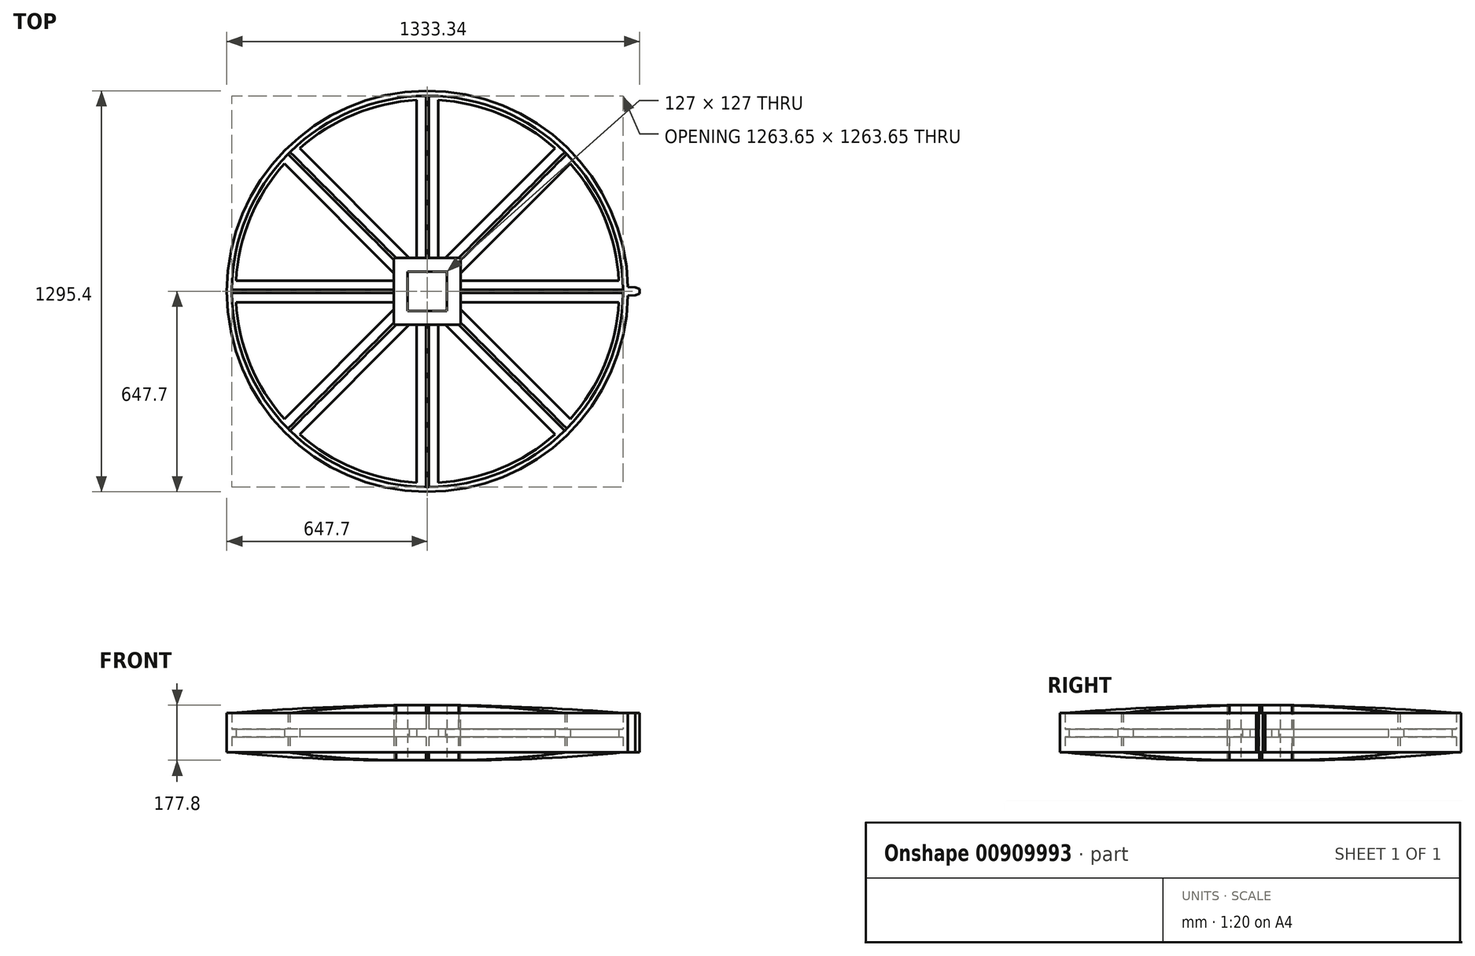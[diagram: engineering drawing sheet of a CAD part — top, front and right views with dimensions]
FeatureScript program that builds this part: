
annotation { "Feature Type Name" : "Feature", "Feature Type Description" : "" }
export const myFeature = defineFeature(function(context is Context, id is Id, definition is map)
    precondition{}
    {
        {
            var Q0;
            Q0=qCreatedBy(makeId("Front.planeOp"),FACE);
            var sketch = newSketch(context, id + "F0", { "sketchPlane" : qUnion([Q0])});
            skLineSegment(sketch, "E0.bottom", {"start": v(0, -88.9) * mm, "end": v(107.95, -88.9) * mm});
            skLineSegment(sketch, "E0.top", {"start": v(0, 88.9) * mm, "end": v(107.95, 88.9) * mm});
            skLineSegment(sketch, "E0.left", {"start": v(0, -88.9) * mm, "end": v(0, 88.9) * mm});
            skLineSegment(sketch, "E0.right", {"start": v(107.95, -88.9) * mm, "end": v(107.95, 88.9) * mm});
            skLineSegment(sketch, "E1.bottom", {"start": v(631.82, -63.5) * mm, "end": v(647.7, -63.5) * mm});
            skLineSegment(sketch, "E1.top", {"start": v(631.82, 63.5) * mm, "end": v(647.7, 63.5) * mm});
            skLineSegment(sketch, "E1.left", {"start": v(631.82, -63.5) * mm, "end": v(631.82, 63.5) * mm});
            skLineSegment(sketch, "E1.right", {"start": v(647.7, -63.5) * mm, "end": v(647.7, 63.5) * mm});
            skLineSegment(sketch, "E2", {"start": v(63.5, 88.9) * mm, "end": v(63.5, -88.9) * mm});
            skLineSegment(sketch, "E3", {"start": v(63.5, 12.5) * mm, "end": v(631.82, 12.5) * mm});
            skLineSegment(sketch, "E4", {"start": v(63.5, -12.9) * mm, "end": v(631.82, -12.9) * mm});
            skLineSegment(sketch, "E5", {"start": v(0, -88.9) * mm, "end": v(0, -224.91) * mm, "construction": true});
            skArc(sketch, "E6", {"start": v(631.82, 63.5) * mm, "mid": v(370.1, 80.7) * mm, "end": v(107.95, 88.9) * mm});
            skPoint(sketch, "E7", {"position": v(0, 0) * mm});
            skLineSegment(sketch, "E8", {"start": v(631.82, 0) * mm, "end": v(0, 0) * mm, "construction": true});
            skArc(sketch, "E9", {"start": v(107.95, -88.9) * mm, "mid": v(370.2, -82.55) * mm, "end": v(631.83, -63.5) * mm});
            skLineSegment(sketch, "E10", {"start": v(619.12, 12.5) * mm, "end": v(619.12, -12.9) * mm});
            skSolve(sketch);
        }
        {
            var Q0;
            {var subQ0=sQuery(id+"F0.wireOp",EDGE,"E0.left");Q0=makeQuery(id+"F0.imprint","IMPRINT",FACE,{"disambiguationData":[TD([[makeQuery(id+"F0.imprint","IMPRINT",EDGE,{"derivedFrom":subQ0}),-1.0]])]});}
            var Q1;
            {var subQ6=sQuery(id+"F0.wireOp",EDGE,"E2");Q1=makeQuery(id+"F0.imprint","IMPRINT",FACE,{"disambiguationData":[TD([[makeQuery(id+"F0.imprint","IMPRINT",EDGE,{"derivedFrom":subQ6}),1.0]])]});}
            var Q2;
            Q2=sQuery(id+"F0.wireOp",EDGE,"E0.left");
            revolve(context, id + "F1", {"surfaceOperationType" : NewSurfaceOperationType.NEW, "entities" : qUnion([Q0, Q1]), "axis" : qUnion([Q2]), "revolveType" : RevolveType.SYMMETRIC, "angle" : 45 * degree});
        }
        {
            var Q0;
            {var subQ0=sQuery(id+"F0.wireOp",EDGE,"E4");var subQ1=sQuery(id+"F0.wireOp",EDGE,"E0.right");var subQ2=makeQuery(id+"F0.imprint","INTERSECT",VERTEX,{"derivedFrom":[subQ1,subQ0]});Q0=makeQuery(id+"F0.imprint","IMPRINT",FACE,{"disambiguationData":[TD([[makeQuery(id+"F0.imprint","IMPRINT",EDGE,{"disambiguationData":[TD([[subQ2,-1.0]])],"derivedFrom":subQ1}),-1.0]])]});}
            var Q1;
            {var subQ0=sQuery(id+"F0.wireOp",EDGE,"E4");var subQ1=sQuery(id+"F0.wireOp",EDGE,"E0.right");var subQ2=makeQuery(id+"F0.imprint","INTERSECT",VERTEX,{"derivedFrom":[subQ1,subQ0]});Q1=makeQuery(id+"F0.imprint","IMPRINT",FACE,{"disambiguationData":[TD([[makeQuery(id+"F0.imprint","IMPRINT",EDGE,{"disambiguationData":[TD([[subQ2,-1.0]])],"derivedFrom":subQ1}),1.0]])]});}
            extrude(context, id + "F2", {"entities" : qUnion([Q0, Q1]), "operationType" : NewBodyOperationType.ADD, "depth" : 69.85 * mm, "offsetDistance" : 25 * mm, "symmetric" : true});
        }
        {
            var Q0;
            {var subQ3=sQuery(id+"F0.wireOp",EDGE,"E1.bottom");Q0=makeQuery(id+"F0.imprint","IMPRINT",FACE,{"disambiguationData":[TD([[makeQuery(id+"F0.imprint","IMPRINT",EDGE,{"derivedFrom":subQ3}),1.0]])]});}
            var Q1;
            {var subQ5=sQuery(id+"F0.wireOp",EDGE,"E10");Q1=makeQuery(id+"F0.imprint","IMPRINT",FACE,{"disambiguationData":[TD([[makeQuery(id+"F0.imprint","IMPRINT",EDGE,{"derivedFrom":subQ5}),1.0]])]});}
            var Q2;
            Q2=sQuery(id+"F0.wireOp",EDGE,"E0.left");
            revolve(context, id + "F3", {"operationType" : NewBodyOperationType.ADD, "surfaceOperationType" : NewSurfaceOperationType.NEW, "entities" : qUnion([Q0, Q1]), "axis" : qUnion([Q2]), "revolveType" : RevolveType.SYMMETRIC, "angle" : 45 * degree});
        }
        {
            var Q0;
            {var subQ1=sQuery(id+"F0.wireOp",EDGE,"E0.top");var subQ3=sQuery(id+"F0.wireOp",EDGE,"E2");var subQ4=makeQuery(id+"F0.imprint","INTERSECT",VERTEX,{"derivedFrom":[subQ1,subQ3]});Q0=makeQuery(id+"F0.imprint","IMPRINT",FACE,{"disambiguationData":[TD([[makeQuery(id+"F0.imprint","IMPRINT",EDGE,{"disambiguationData":[TD([[subQ4,-1.0]])],"derivedFrom":subQ3}),1.0]])]});}
            var Q1;
            {var subQ1=sQuery(id+"F0.wireOp",EDGE,"E0.bottom");var subQ3=sQuery(id+"F0.wireOp",EDGE,"E2");var subQ4=makeQuery(id+"F0.imprint","INTERSECT",VERTEX,{"derivedFrom":[subQ1,subQ3]});Q1=makeQuery(id+"F0.imprint","IMPRINT",FACE,{"disambiguationData":[TD([[makeQuery(id+"F0.imprint","IMPRINT",EDGE,{"disambiguationData":[TD([[subQ4,1.0]])],"derivedFrom":subQ3}),1.0]])]});}
            var Q2;
            {var subQ0=sQuery(id+"F0.wireOp",EDGE,"E6");Q2=makeQuery(id+"F0.imprint","IMPRINT",FACE,{"disambiguationData":[TD([[makeQuery(id+"F0.imprint","IMPRINT",EDGE,{"derivedFrom":subQ0}),1.0]])]});}
            var Q3;
            {var subQ0=sQuery(id+"F0.wireOp",EDGE,"E9");Q3=makeQuery(id+"F0.imprint","IMPRINT",FACE,{"disambiguationData":[TD([[makeQuery(id+"F0.imprint","IMPRINT",EDGE,{"derivedFrom":subQ0}),1.0]])]});}
            extrude(context, id + "F4", {"entities" : qUnion([Q0, Q1, Q2, Q3]), "operationType" : NewBodyOperationType.ADD, "depth" : 9.53 * mm, "offsetDistance" : 25 * mm, "symmetric" : true});
        }
        {
            var Q0;
            Q0=makeQuery(id+"F1.opRevolve","SWEPT_BODY",BODY,{"disambiguationData":[OSD([sQuery(id+"F0.wireOp",EDGE,"E0.bottom"),sQuery(id+"F0.wireOp",EDGE,"E0.top"),sQuery(id+"F0.wireOp",EDGE,"E0.left"),sQuery(id+"F0.wireOp",EDGE,"E0.right")])]});
            var Q1;
            Q1=sQuery(id+"F0.wireOp",EDGE,"E0.left");
            circularPattern(context, id + "F5", {"operationType" : NewBodyOperationType.ADD, "entities" : qUnion([Q0]), "axis" : qUnion([Q1]), "angle" : 360 * degree, "instanceCount" : 8, "equalSpace" : true});
        }
        {
            var Q0;
            {var subQ0=makeQuery(id+"F3.opRevolve","SWEPT_FACE",FACE,{"disambiguationData":[OSD([sQuery(id+"F0.wireOp",EDGE,"E1.top")])]});Q0=makeQuery(id+"F5.boolean.opBoolean","MERGE",FACE,{"derivedFrom":[subQ0,makeQuery(id+"F5.opPattern","COPY",FACE,{"derivedFrom":subQ0,"instanceName":"1"}),makeQuery(id+"F5.opPattern","COPY",FACE,{"derivedFrom":subQ0,"instanceName":"2"}),makeQuery(id+"F5.opPattern","COPY",FACE,{"derivedFrom":subQ0,"instanceName":"3"}),makeQuery(id+"F5.opPattern","COPY",FACE,{"derivedFrom":subQ0,"instanceName":"4"}),makeQuery(id+"F5.opPattern","COPY",FACE,{"derivedFrom":subQ0,"instanceName":"5"}),makeQuery(id+"F5.opPattern","COPY",FACE,{"derivedFrom":subQ0,"instanceName":"6"}),makeQuery(id+"F5.opPattern","COPY",FACE,{"derivedFrom":subQ0,"instanceName":"7"})]});}
            var sketch = newSketch(context, id + "F6", { "sketchPlane" : qUnion([Q0])});
            skLineSegment(sketch, "E11", {"start": v(647.54, 14.29) * mm, "end": v(671.86, 12.16) * mm});
            skLineSegment(sketch, "E12", {"start": v(671.86, 12.16) * mm, "end": v(685.64, 7.14) * mm});
            skLineSegment(sketch, "E13", {"start": v(685.64, 7.14) * mm, "end": v(685.64, -7.14) * mm});
            skLineSegment(sketch, "E14", {"start": v(685.64, -7.14) * mm, "end": v(671.86, -12.16) * mm});
            skLineSegment(sketch, "E15", {"start": v(671.86, -12.16) * mm, "end": v(647.54, -14.29) * mm});
            skLineSegment(sketch, "E16", {"start": v(0, 0) * mm, "end": v(685.64, 0) * mm, "construction": true});
            skLineSegment(sketch, "E17", {"start": v(647.54, 14.29) * mm, "end": v(647.54, -14.29) * mm});
            skSolve(sketch);
        }
        {
            var Q0;
            {var subQ0=sQuery(id+"F6.wireOp",EDGE,"E11");Q0=makeQuery(id+"F6.imprint","IMPRINT",FACE,{"disambiguationData":[TD([[makeQuery(id+"F6.imprint","IMPRINT",EDGE,{"derivedFrom":subQ0}),-1.0]])]});}
            var Q1;
            {var subQ0=sQuery(id+"F0.wireOp",EDGE,"E0.bottom");var subQ1=makeQuery(id+"F4.boolean.opBoolean","MERGE",FACE,{"derivedFrom":[makeQuery(id+"F1.opRevolve","SWEPT_FACE",FACE,{"disambiguationData":[OSD([subQ0])]}),makeQuery(id+"F3.opRevolve","SWEPT_FACE",FACE,{"disambiguationData":[OSD([sQuery(id+"F0.wireOp",EDGE,"E1.bottom")])]}),makeQuery(id+"F4.opExtrude","SWEPT_FACE",FACE,{"disambiguationData":[OSD([subQ0,sQuery(id+"F0.wireOp",EDGE,"D5k9asr0-8ta1-f4uu-XxQ3-tXAVFih4KlHv")])]})]});Q1=makeQuery(id+"F5.boolean.opBoolean","MERGE",FACE,{"derivedFrom":[subQ1,makeQuery(id+"F5.opPattern","COPY",FACE,{"derivedFrom":subQ1,"instanceName":"1"}),makeQuery(id+"F5.opPattern","COPY",FACE,{"derivedFrom":subQ1,"instanceName":"2"}),makeQuery(id+"F5.opPattern","COPY",FACE,{"derivedFrom":subQ1,"instanceName":"3"}),makeQuery(id+"F5.opPattern","COPY",FACE,{"derivedFrom":subQ1,"instanceName":"4"}),makeQuery(id+"F5.opPattern","COPY",FACE,{"derivedFrom":subQ1,"instanceName":"5"}),makeQuery(id+"F5.opPattern","COPY",FACE,{"derivedFrom":subQ1,"instanceName":"6"}),makeQuery(id+"F5.opPattern","COPY",FACE,{"derivedFrom":subQ1,"instanceName":"7"})]});}
            extrude(context, id + "F7", {"entities" : qUnion([Q0]), "operationType" : NewBodyOperationType.ADD, "oppositeDirection" : true, "depth" : 127 * mm, "endBoundEntityFace" : qUnion([Q1]), "offsetDistance" : 25 * mm});
        }
        {
            var Q0;
            {var subQ0=sQuery(id+"F0.wireOp",EDGE,"E0.bottom");var subQ1=makeQuery(id+"F4.boolean.opBoolean","MERGE",FACE,{"derivedFrom":[makeQuery(id+"F1.opRevolve","SWEPT_FACE",FACE,{"disambiguationData":[OSD([subQ0])]}),makeQuery(id+"F3.opRevolve","SWEPT_FACE",FACE,{"disambiguationData":[OSD([sQuery(id+"F0.wireOp",EDGE,"E1.bottom")])]}),makeQuery(id+"F4.opExtrude","SWEPT_FACE",FACE,{"disambiguationData":[OSD([subQ0,sQuery(id+"F0.wireOp",EDGE,"D5k9asr0-8ta1-f4uu-XxQ3-tXAVFih4KlHv")])]})]});Q0=makeQuery(id+"F5.boolean.opBoolean","MERGE",FACE,{"derivedFrom":[subQ1,makeQuery(id+"F5.opPattern","COPY",FACE,{"derivedFrom":subQ1,"instanceName":"1"}),makeQuery(id+"F5.opPattern","COPY",FACE,{"derivedFrom":subQ1,"instanceName":"2"}),makeQuery(id+"F5.opPattern","COPY",FACE,{"derivedFrom":subQ1,"instanceName":"3"}),makeQuery(id+"F5.opPattern","COPY",FACE,{"derivedFrom":subQ1,"instanceName":"4"}),makeQuery(id+"F5.opPattern","COPY",FACE,{"derivedFrom":subQ1,"instanceName":"5"}),makeQuery(id+"F5.opPattern","COPY",FACE,{"derivedFrom":subQ1,"instanceName":"6"}),makeQuery(id+"F5.opPattern","COPY",FACE,{"derivedFrom":subQ1,"instanceName":"7"})]});}
            var sketch = newSketch(context, id + "F8", { "sketchPlane" : qUnion([Q0])});
            skLineSegment(sketch, "E18.bottom", {"start": v(-63.5, 63.5) * mm, "end": v(63.5, 63.5) * mm});
            skLineSegment(sketch, "E18.top", {"start": v(-63.5, -63.5) * mm, "end": v(63.5, -63.5) * mm});
            skLineSegment(sketch, "E18.left", {"start": v(-63.5, 63.5) * mm, "end": v(-63.5, -63.5) * mm});
            skLineSegment(sketch, "E18.right", {"start": v(63.5, 63.5) * mm, "end": v(63.5, -63.5) * mm});
            skLineSegment(sketch, "E19", {"start": v(-63.5, 63.5) * mm, "end": v(63.5, -63.5) * mm, "construction": true});
            skLineSegment(sketch, "E20", {"start": v(63.5, 63.5) * mm, "end": v(-63.5, -63.5) * mm, "construction": true});
            skLineSegment(sketch, "E21.bottom", {"start": v(-107.95, -107.95) * mm, "end": v(107.95, -107.95) * mm});
            skLineSegment(sketch, "E21.top", {"start": v(-107.95, 107.95) * mm, "end": v(107.95, 107.95) * mm});
            skLineSegment(sketch, "E21.left", {"start": v(-107.95, -107.95) * mm, "end": v(-107.95, 107.95) * mm});
            skLineSegment(sketch, "E21.right", {"start": v(107.95, -107.95) * mm, "end": v(107.95, 107.95) * mm});
            skSolve(sketch);
        }
        {
            var Q0;
            {var subQ2=sQuery(id+"F0.wireOp",EDGE,"E0.bottom");var subQ3=makeQuery(id+"F4.opExtrude","CAP_EDGE",EDGE,{"disambiguationData":[OSD([subQ2])],"isStart":true});var subQ4=makeQuery(id+"F5.opPattern","COPY",EDGE,{"derivedFrom":subQ3,"instanceName":"2"});Q0=makeQuery(id+"F8.imprint","IMPRINT",FACE,{"disambiguationData":[TD([[makeQuery(id+"F8.imprint","IMPRINT",EDGE,{"derivedFrom":subQ4}),-1.0]])]});}
            var Q1;
            {var subQ2=sQuery(id+"F0.wireOp",EDGE,"E0.bottom");var subQ3=makeQuery(id+"F4.opExtrude","CAP_EDGE",EDGE,{"disambiguationData":[OSD([subQ2])],"isStart":true});var subQ4=makeQuery(id+"F5.opPattern","COPY",EDGE,{"derivedFrom":subQ3,"instanceName":"4"});Q1=makeQuery(id+"F8.imprint","IMPRINT",FACE,{"disambiguationData":[TD([[makeQuery(id+"F8.imprint","IMPRINT",EDGE,{"derivedFrom":subQ4}),-1.0]])]});}
            var Q2;
            {var subQ0=sQuery(id+"F0.wireOp",EDGE,"E0.bottom");var subQ3=makeQuery(id+"F4.opExtrude","CAP_EDGE",EDGE,{"disambiguationData":[OSD([subQ0])],"isStart":false});Q2=makeQuery(id+"F8.imprint","IMPRINT",FACE,{"disambiguationData":[TD([[makeQuery(id+"F8.imprint","IMPRINT",EDGE,{"derivedFrom":subQ3}),1.0]])]});}
            var Q3;
            {var subQ2=sQuery(id+"F0.wireOp",EDGE,"E0.bottom");var subQ4=makeQuery(id+"F4.opExtrude","CAP_EDGE",EDGE,{"disambiguationData":[OSD([subQ2])],"isStart":true});Q3=makeQuery(id+"F8.imprint","IMPRINT",FACE,{"disambiguationData":[TD([[makeQuery(id+"F8.imprint","IMPRINT",EDGE,{"derivedFrom":subQ4}),-1.0]])]});}
            var Q4;
            Q4=makeQuery(id+"F8.imprint","IMPRINT",FACE,{"disambiguationData":[TD([[makeQuery(id+"F8.imprint","IMPRINT",EDGE,{"derivedFrom":sQuery(id+"F8.wireOp",EDGE,"E18.bottom")}),1.0]])]});
            extrude(context, id + "F9", {"entities" : qUnion([Q0, Q1, Q2, Q3, Q4]), "operationType" : NewBodyOperationType.ADD, "oppositeDirection" : true, "depth" : 177.8 * mm, "offsetDistance" : 25 * mm});
        }
        {
            var Q0;
            Q0=makeQuery(id+"F8.imprint","IMPRINT",FACE,{"disambiguationData":[TD([[makeQuery(id+"F8.imprint","IMPRINT",EDGE,{"derivedFrom":sQuery(id+"F8.wireOp",EDGE,"E18.bottom")}),-1.0]])]});
            extrude(context, id + "F10", {"entities" : qUnion([Q0]), "operationType" : NewBodyOperationType.REMOVE, "oppositeDirection" : true, "depth" : 508 * mm, "offsetDistance" : 25 * mm, "symmetric" : true});
        }
    });
